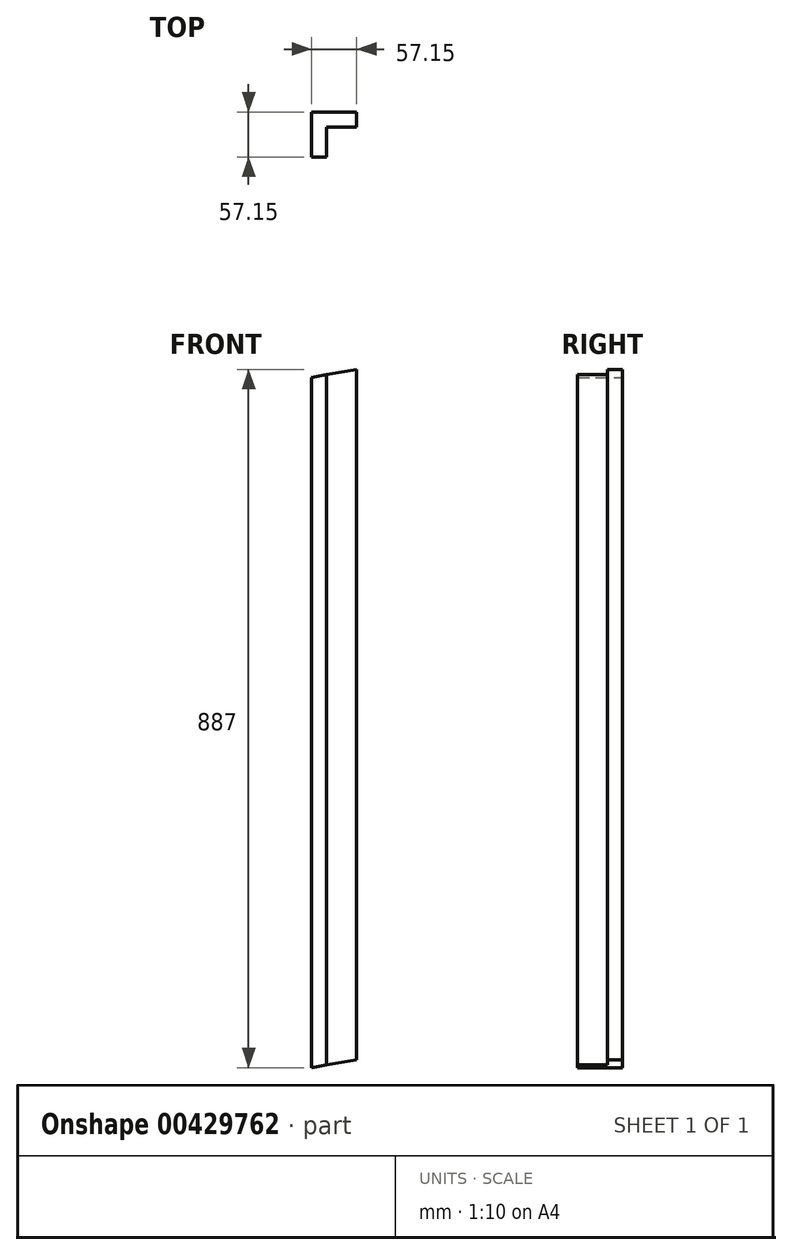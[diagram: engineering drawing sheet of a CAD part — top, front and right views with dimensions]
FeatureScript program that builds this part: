
annotation { "Feature Type Name" : "Feature", "Feature Type Description" : "" }
export const myFeature = defineFeature(function(context is Context, id is Id, definition is map)
    precondition{}
    {
        {
            var Q0;
            Q0=qCreatedBy(makeId("Top.planeOp"),FACE);
            var sketch = newSketch(context, id + "F0", { "sketchPlane" : qUnion([Q0])});
            skLineSegment(sketch, "E0", {"start": v(0, 0) * mm, "end": v(57.15, 0) * mm});
            skLineSegment(sketch, "E1", {"start": v(57.15, 0) * mm, "end": v(57.15, -19.05) * mm});
            skLineSegment(sketch, "E2", {"start": v(57.15, -19.05) * mm, "end": v(19.05, -19.05) * mm});
            skLineSegment(sketch, "E3", {"start": v(19.05, -19.05) * mm, "end": v(19.05, -57.15) * mm});
            skLineSegment(sketch, "E4", {"start": v(19.05, -57.15) * mm, "end": v(0, -57.15) * mm});
            skLineSegment(sketch, "E5", {"start": v(0, -57.15) * mm, "end": v(0, 0) * mm});
            skSolve(sketch);
        }
        {
            var Q0;
            Q0=qSketchRegion(id+"F0",true);
            extrude(context, id + "F1", {"entities" : qUnion([Q0]), "depth" : 1016 * mm});
        }
        {
            var Q0;
            Q0=makeQuery(id+"F1.opExtrude","SWEPT_FACE",FACE,{"disambiguationData":[OSD([sQuery(id+"F0.wireOp",EDGE,"E0")])]});
            var sketch = newSketch(context, id + "F2", { "sketchPlane" : qUnion([Q0])});
            skLineSegment(sketch, "E6", {"start": v(0, 0) * mm, "end": v(-57.15, 0) * mm});
            skLineSegment(sketch, "E7", {"start": v(0, 1016) * mm, "end": v(-57.15, 1016) * mm});
            skLineSegment(sketch, "E8", {"start": v(-57.15, 1016) * mm, "end": v(-57.15, 887) * mm});
            skLineSegment(sketch, "E9", {"start": v(-57.15, 887) * mm, "end": v(0, 876.92) * mm});
            skLineSegment(sketch, "E10", {"start": v(0, 876.92) * mm, "end": v(0, 1016) * mm});
            skLineSegment(sketch, "E11", {"start": v(0, 0) * mm, "end": v(-57.15, 10.08) * mm});
            skLineSegment(sketch, "E12", {"start": v(-57.15, 10.08) * mm, "end": v(-57.15, 0) * mm});
            skSolve(sketch);
        }
        {
            var Q0;
            Q0=qSketchRegion(id+"F2",true);
            extrude(context, id + "F3", {"entities" : qUnion([Q0]), "operationType" : NewBodyOperationType.REMOVE, "endBound" : BoundingType.THROUGH_ALL, "oppositeDirection" : true, "depth" : 25.4 * mm});
        }
    });
